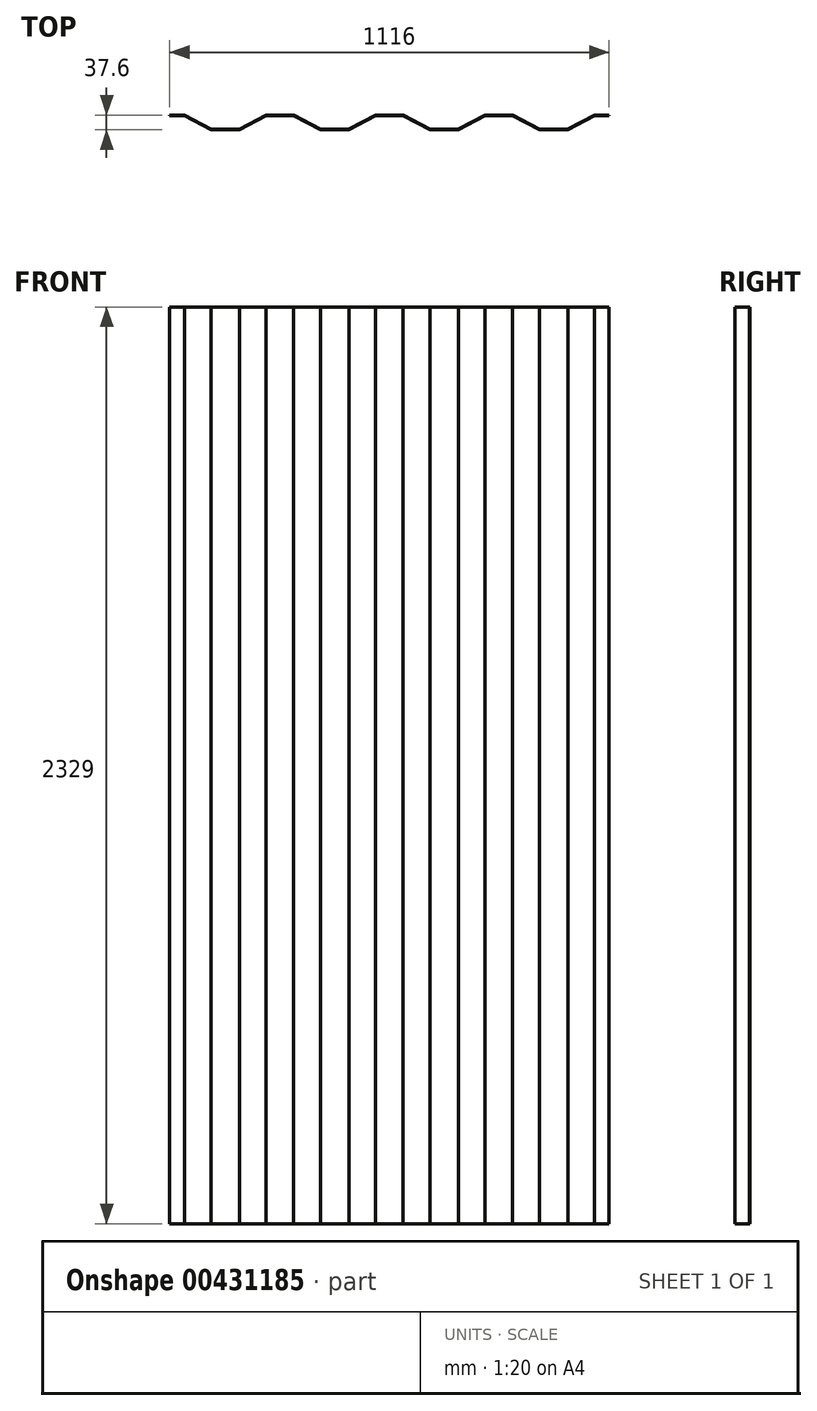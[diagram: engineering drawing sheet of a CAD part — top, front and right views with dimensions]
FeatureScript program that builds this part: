
annotation { "Feature Type Name" : "Feature", "Feature Type Description" : "" }
export const myFeature = defineFeature(function(context is Context, id is Id, definition is map)
    precondition{}
    {
        {
            var Q0;
            Q0=qCreatedBy(makeId("Top.planeOp"),FACE);
            var sketch = newSketch(context, id + "F0", { "sketchPlane" : qUnion([Q0])});
            skPoint(sketch, "E0", {"position": v(0, -36) * mm});
            skPoint(sketch, "E1", {"position": v(37, -36) * mm});
            skPoint(sketch, "E2", {"position": v(245, -36) * mm});
            skLineSegment(sketch, "E3", {"start": v(0, 0) * mm, "end": v(37, 0) * mm});
            skLineSegment(sketch, "E4", {"start": v(37, 0) * mm, "end": v(105, -36) * mm});
            skLineSegment(sketch, "E5", {"start": v(177, -36) * mm, "end": v(105, -36) * mm});
            skLineSegment(sketch, "E6", {"start": v(177, -36) * mm, "end": v(245, 0) * mm});
            skLineSegment(sketch, "E7", {"start": v(245, 0) * mm, "end": v(315, 0) * mm});
            skLineSegment(sketch, "E8.0", {"start": v(0, 1.6) * mm, "end": v(37.4, 1.6) * mm});
            skLineSegment(sketch, "E9", {"start": v(0, 0) * mm, "end": v(0, 1.6) * mm});
            skLineSegment(sketch, "E10.0", {"start": v(37.4, 1.6) * mm, "end": v(105.4, -34.4) * mm});
            skLineSegment(sketch, "E11.0", {"start": v(176.6, -34.4) * mm, "end": v(105.4, -34.4) * mm});
            skLineSegment(sketch, "E12.0", {"start": v(176.6, -34.4) * mm, "end": v(244.6, 1.6) * mm});
            skLineSegment(sketch, "E13.0", {"start": v(244.6, 1.6) * mm, "end": v(315.4, 1.6) * mm});
            skLineSegment(sketch, "E14", {"start": v(315, 0) * mm, "end": v(383, -36) * mm});
            skLineSegment(sketch, "E15", {"start": v(455, -36) * mm, "end": v(383, -36) * mm});
            skLineSegment(sketch, "E16", {"start": v(455, -36) * mm, "end": v(523, 0) * mm});
            skLineSegment(sketch, "E17", {"start": v(523, 0) * mm, "end": v(593, 0) * mm});
            skLineSegment(sketch, "E18.0", {"start": v(315.4, 1.6) * mm, "end": v(383.4, -34.4) * mm});
            skLineSegment(sketch, "E19.0", {"start": v(454.6, -34.4) * mm, "end": v(383.4, -34.4) * mm});
            skLineSegment(sketch, "E20.0", {"start": v(454.6, -34.4) * mm, "end": v(522.6, 1.6) * mm});
            skLineSegment(sketch, "E21.0", {"start": v(522.6, 1.6) * mm, "end": v(593.4, 1.6) * mm});
            skLineSegment(sketch, "E22", {"start": v(593, 0) * mm, "end": v(661, -36) * mm});
            skLineSegment(sketch, "E23", {"start": v(733, -36) * mm, "end": v(661, -36) * mm});
            skLineSegment(sketch, "E24", {"start": v(733, -36) * mm, "end": v(801, 0) * mm});
            skLineSegment(sketch, "E25", {"start": v(801, 0) * mm, "end": v(871, 0) * mm});
            skLineSegment(sketch, "E26.0", {"start": v(593.4, 1.6) * mm, "end": v(661.4, -34.4) * mm});
            skLineSegment(sketch, "E27.0", {"start": v(732.6, -34.4) * mm, "end": v(661.4, -34.4) * mm});
            skLineSegment(sketch, "E28.0", {"start": v(732.6, -34.4) * mm, "end": v(800.6, 1.6) * mm});
            skLineSegment(sketch, "E29.0", {"start": v(800.6, 1.6) * mm, "end": v(871.4, 1.6) * mm});
            skLineSegment(sketch, "E30", {"start": v(871, 0) * mm, "end": v(939, -36) * mm});
            skLineSegment(sketch, "E31", {"start": v(1011, -36) * mm, "end": v(939, -36) * mm});
            skLineSegment(sketch, "E32", {"start": v(1011, -36) * mm, "end": v(1079, 0) * mm});
            skLineSegment(sketch, "E33", {"start": v(1079, 0) * mm, "end": v(1116, 0) * mm});
            skLineSegment(sketch, "E34.0", {"start": v(871.4, 1.6) * mm, "end": v(939.4, -34.4) * mm});
            skLineSegment(sketch, "E35.0", {"start": v(1010.6, -34.4) * mm, "end": v(939.4, -34.4) * mm});
            skLineSegment(sketch, "E36.0", {"start": v(1010.6, -34.4) * mm, "end": v(1078.6, 1.6) * mm});
            skLineSegment(sketch, "E37.0", {"start": v(1078.6, 1.6) * mm, "end": v(1116, 1.6) * mm});
            skLineSegment(sketch, "E38", {"start": v(1116, 0) * mm, "end": v(1116, 1.6) * mm});
            skSolve(sketch);
        }
        {
            var Q0;
            Q0 = qSketchRegion(id + "F0", true);
            extrude(context, id + "F1", {"entities" : qUnion([Q0]), "depth" : 2329 * mm});
        }
    });
